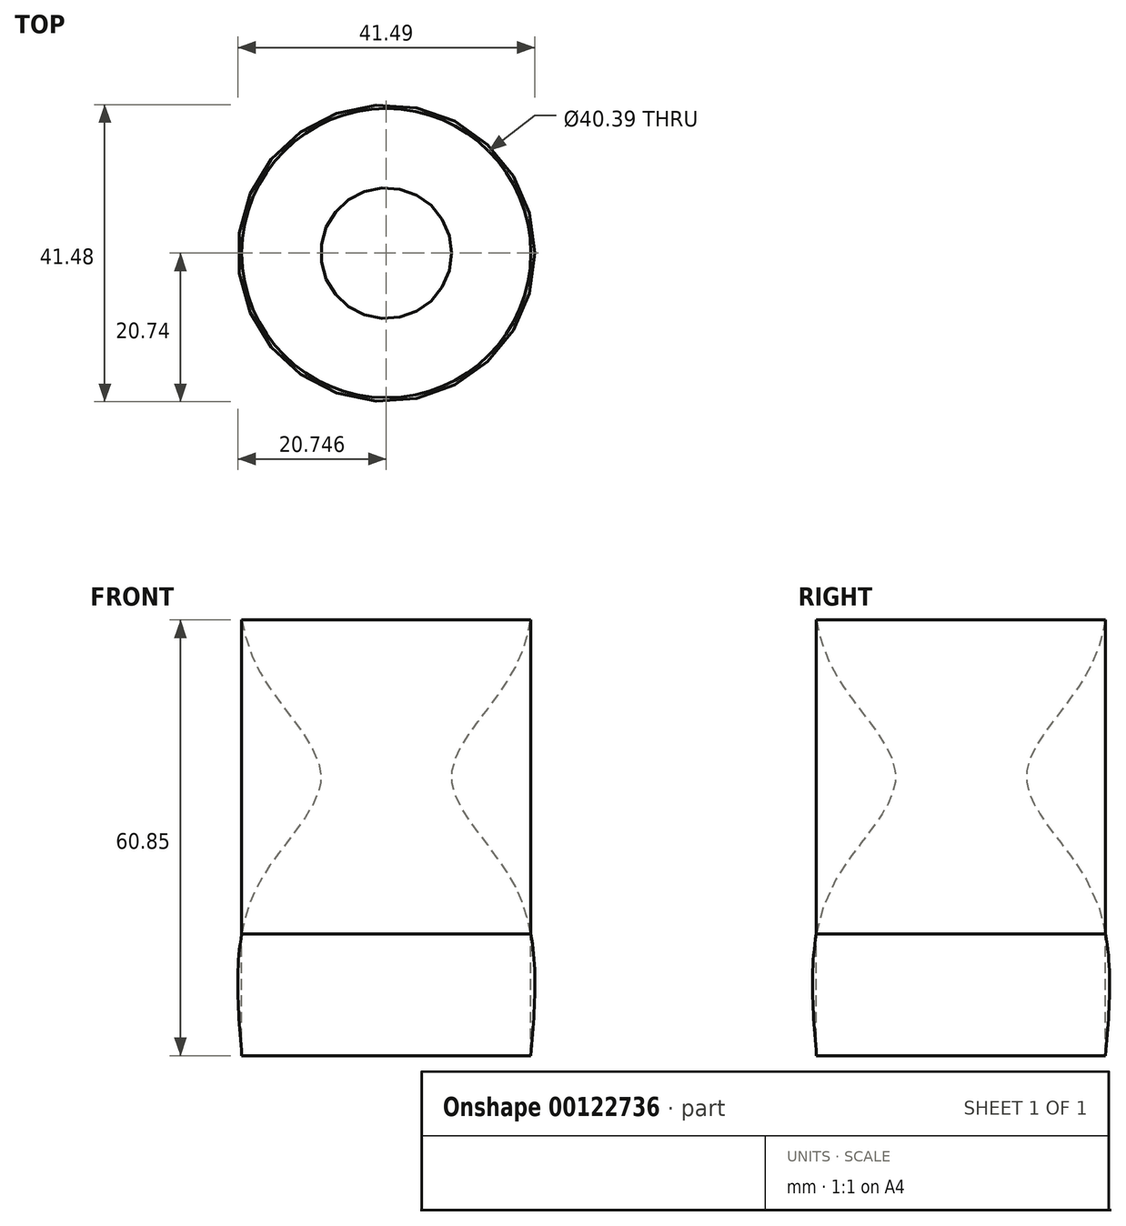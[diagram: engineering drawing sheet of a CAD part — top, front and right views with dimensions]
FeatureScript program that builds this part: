
annotation { "Feature Type Name" : "Feature", "Feature Type Description" : "" }
export const myFeature = defineFeature(function(context is Context, id is Id, definition is map)
    precondition{}
    {
        {
            var Q0;
            Q0=qCreatedBy(makeId("Front.planeOp"),FACE);
            var sketch = newSketch(context, id + "F0", { "sketchPlane" : qUnion([Q0])});
            skPoint(sketch, "E0.visualSharp", {"position": v(-22.5, 51.22) * mm});
            skPoint(sketch, "E1.visualSharp", {"position": v(-22.5, 20.08) * mm});
            skLineSegment(sketch, "E2", {"start": v(-20.46, 57.57) * mm, "end": v(-20.46, -54.43) * mm});
            skFitSpline(sketch, "E3", {"points": [v(-20.46, -3.28) * mm, v(-22.5, 20.08) * mm, v(-31.52, 35.65) * mm, v(-22.5, 51.22) * mm, v(-20.46, 74.58) * mm], "startDerivative": vector(7.58, 93.23) * mm, "endDerivative": vector(-7.57, 93.23) * mm});
            skLineSegment(sketch, "E4", {"start": v(-40.65, 57.57) * mm, "end": v(-40.65, -54.43) * mm, "construction": true});
            skLineSegment(sketch, "E5", {"start": v(-20.46, 57.57) * mm, "end": v(-40.65, 57.57) * mm, "construction": true});
            skSolve(sketch);
        }
        {
            var Q0;
            Q0 = qSketchRegion(id + "F0", true);
            var Q1;
            Q1=sQuery(id+"F0.wireOp",EDGE,"E4");
            revolve(context, id + "F1", {"entities" : qUnion([Q0]), "axis" : qUnion([Q1]), "revolveType" : RevolveType.FULL});
        }
    });
